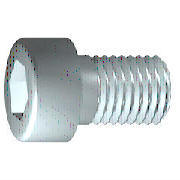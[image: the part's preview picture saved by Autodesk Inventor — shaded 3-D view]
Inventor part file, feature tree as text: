
AUTODESK INVENTOR PART (.ipt)
format: ipt  version: 2024.3 (Build 283343000, 343)  size: 194,048 bytes
history: native  units: mm (DEFAULTED — no unit token found)
features: extrude x1, plane x1, fillet x1
ambient origin geometry x7: Origin, YZ Plane, XY Plane, X Axis, Y Axis, Z Axis, Center Point
bodies: Solid1 (feature_tree), Body (feature_tree)
feature tree (3):
  extrude  "Slot"  Depth=10.25mm
  plane  "Work Plane1"
  fillet  "Fillet2"  Radius=0.429515mm
